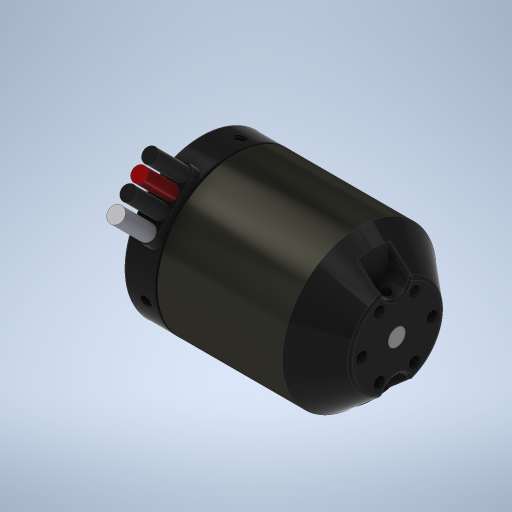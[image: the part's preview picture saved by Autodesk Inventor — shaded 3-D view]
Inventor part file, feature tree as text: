
AUTODESK INVENTOR PART (.ipt)
format: ipt  version: 2024.2 (Build 282272000, 272)  size: 3,438,592 bytes
history: native  units: in
note: dims shown in document units (in); Inventor stores cm internally (conversion verified against a paired STEP export)
features: thread x13, other x1
ambient origin geometry x8: Origin, YZ Plane, XZ Plane, XY Plane, X Axis, Y Axis, Z Axis, Center Point
bodies: Solid1 (feature_tree)
feature tree (14):
  thread  "Thread1"  [1 undecoded]
  thread  "Thread2"  [1 undecoded]
  thread  "Thread3"  [1 undecoded]
  thread  "Thread4"  [1 undecoded]
  thread  "Thread5"  [1 undecoded]
  thread  "Thread6"  [1 undecoded]
  thread  "Thread7"  [1 undecoded]
  thread  "Thread8"  [1 undecoded]
  thread  "Thread9"  [1 undecoded]
  thread  "Thread10"  [1 undecoded]
  thread  "Thread11"  [1 undecoded]
  thread  "Thread12"  [1 undecoded]
  thread  "Thread13"  [1 undecoded]
  other  "Wrap2"
note: 13 required parameter values undecoded (feature->parameter linkage not recoverable at this tier; creation-order binding heuristic only, values carry confidence <= 0.55)
